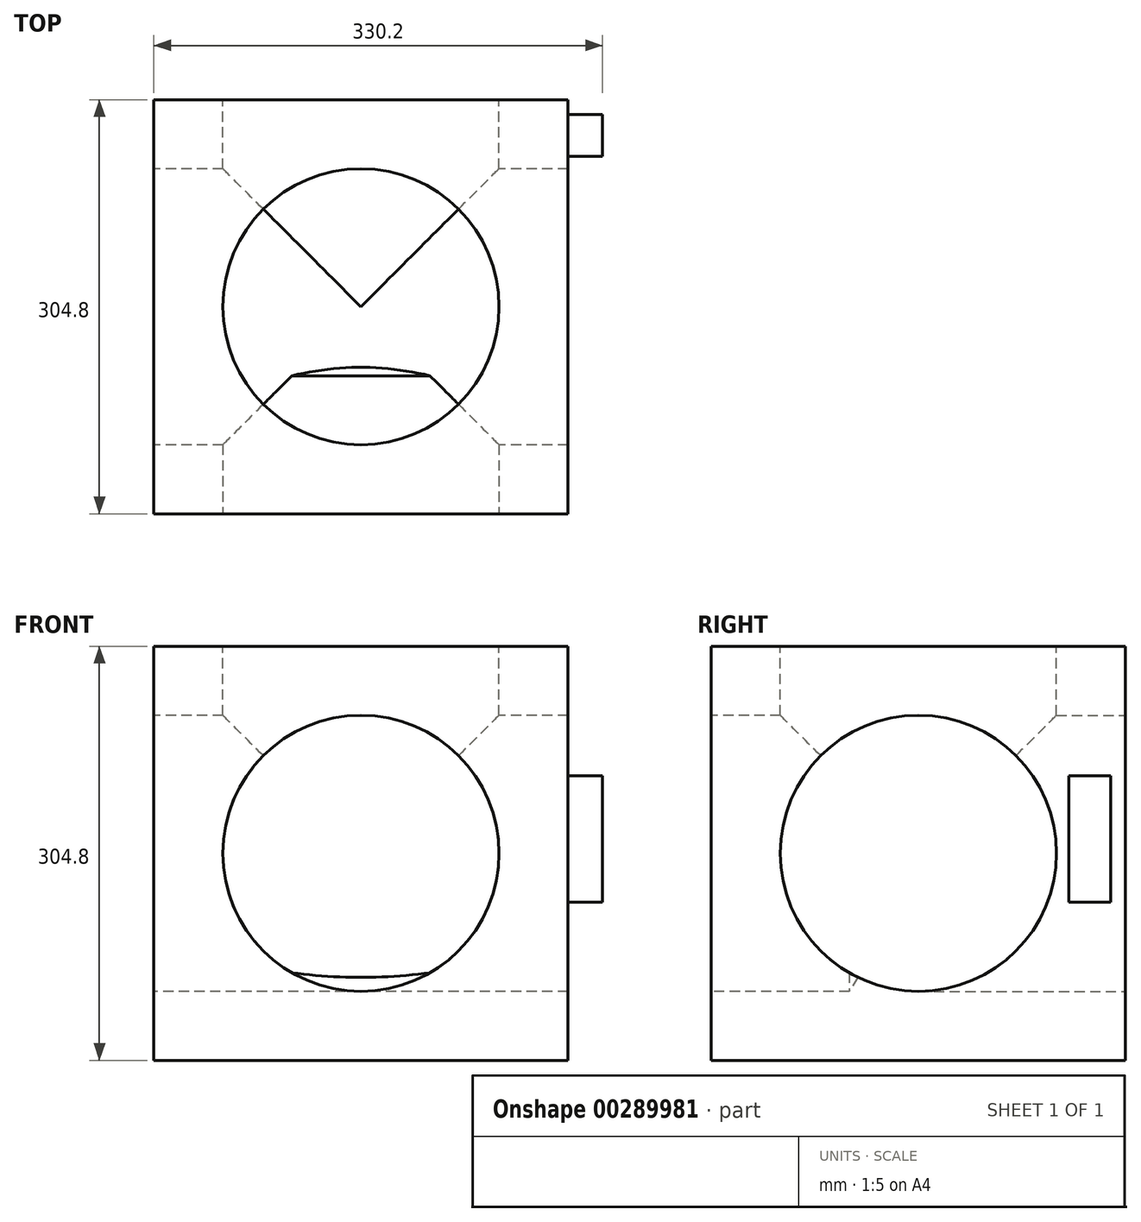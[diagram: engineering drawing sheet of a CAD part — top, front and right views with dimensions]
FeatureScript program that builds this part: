
annotation { "Feature Type Name" : "Feature", "Feature Type Description" : "" }
export const myFeature = defineFeature(function(context is Context, id is Id, definition is map)
    precondition{}
    {
        {
            var Q0;
            Q0=qCreatedBy(makeId("Top.planeOp"),FACE);
            var sketch = newSketch(context, id + "F0", { "sketchPlane" : qUnion([Q0])});
            skLineSegment(sketch, "E0.bottom", {"start": v(-154.31, 197.67) * mm, "end": v(150.49, 197.67) * mm});
            skLineSegment(sketch, "E0.top", {"start": v(-154.31, -107.13) * mm, "end": v(150.49, -107.13) * mm});
            skLineSegment(sketch, "E0.left", {"start": v(-154.31, 197.67) * mm, "end": v(-154.31, -107.13) * mm});
            skLineSegment(sketch, "E0.right", {"start": v(150.49, 197.67) * mm, "end": v(150.49, -107.13) * mm});
            skSolve(sketch);
        }
        {
            var Q0;
            Q0 = qSketchRegion(id + "F0", true);
            extrude(context, id + "F1", {"entities" : qUnion([Q0]), "depth" : 304.8 * mm});
        }
        {
            var Q0;
            Q0=makeQuery(id+"F1.opExtrude","SWEPT_FACE",FACE,{"disambiguationData":[OSD([sQuery(id+"F0.wireOp",EDGE,"E0.top")])]});
            var sketch = newSketch(context, id + "F2", { "sketchPlane" : qUnion([Q0])});
            skCircle(sketch, "E1", {"center": v(-1.91, 152.4) * mm, "radius": 101.6 * mm});
            skSolve(sketch);
        }
        {
            var Q0;
            Q0=sQuery(id+"F2.wireOp",VERTEX,"E1.center");
            var Q1;
            Q1=makeQuery(id+"F1.opExtrude","SWEPT_BODY",BODY,{"disambiguationData":[OSD([sQuery(id+"F0.wireOp",EDGE,"E0.bottom"),sQuery(id+"F0.wireOp",EDGE,"E0.top"),sQuery(id+"F0.wireOp",EDGE,"E0.left"),sQuery(id+"F0.wireOp",EDGE,"E0.right")])]});
            hole(context, id + "F3", {"style" : HoleStyle.SIMPLE, "endStyle" : HoleEndStyle.BLIND, "holeDiameter" : 203.2 * mm, "holeDepth" : 101.6 * mm, "tappedDepth" : 12.7 * mm, "tapClearance" : 3, "startFromSketch" : true, "locations" : qUnion([Q0]), "scope" : qUnion([Q1])});
        }
        {
            var Q0;
            Q0=makeQuery(id+"F1.opExtrude","CAP_FACE",FACE,{"disambiguationData":[OSD([sQuery(id+"F0.wireOp",EDGE,"E0.bottom"),sQuery(id+"F0.wireOp",EDGE,"E0.top"),sQuery(id+"F0.wireOp",EDGE,"E0.left"),sQuery(id+"F0.wireOp",EDGE,"E0.right")])],"isStart":false});
            var sketch = newSketch(context, id + "F4", { "sketchPlane" : qUnion([Q0])});
            skCircle(sketch, "E2", {"center": v(-1.91, 45.27) * mm, "radius": 101.6 * mm});
            skSolve(sketch);
        }
        {
            var Q0;
            Q0=sQuery(id+"F4.wireOp",VERTEX,"E2.center");
            var Q1;
            Q1=makeQuery(id+"F1.opExtrude","SWEPT_BODY",BODY,{"disambiguationData":[OSD([sQuery(id+"F0.wireOp",EDGE,"E0.bottom"),sQuery(id+"F0.wireOp",EDGE,"E0.top"),sQuery(id+"F0.wireOp",EDGE,"E0.left"),sQuery(id+"F0.wireOp",EDGE,"E0.right")])]});
            hole(context, id + "F5", {"style" : HoleStyle.SIMPLE, "endStyle" : HoleEndStyle.BLIND, "holeDiameter" : 203.2 * mm, "holeDepth" : 152.4 * mm, "tappedDepth" : 12.7 * mm, "tapClearance" : 3, "startFromSketch" : true, "locations" : qUnion([Q0]), "scope" : qUnion([Q1])});
        }
        {
            var Q0;
            Q0=makeQuery(id+"F1.opExtrude","SWEPT_FACE",FACE,{"disambiguationData":[OSD([sQuery(id+"F0.wireOp",EDGE,"E0.left")])]});
            var sketch = newSketch(context, id + "F6", { "sketchPlane" : qUnion([Q0])});
            skCircle(sketch, "E3", {"center": v(-45.27, 152.4) * mm, "radius": 101.6 * mm});
            skSolve(sketch);
        }
        {
            var Q0;
            Q0=sQuery(id+"F6.wireOp",VERTEX,"E3.center");
            var Q1;
            Q1=makeQuery(id+"F1.opExtrude","SWEPT_BODY",BODY,{"disambiguationData":[OSD([sQuery(id+"F0.wireOp",EDGE,"E0.bottom"),sQuery(id+"F0.wireOp",EDGE,"E0.top"),sQuery(id+"F0.wireOp",EDGE,"E0.left"),sQuery(id+"F0.wireOp",EDGE,"E0.right")])]});
            hole(context, id + "F7", {"style" : HoleStyle.SIMPLE, "endStyle" : HoleEndStyle.BLIND, "holeDiameter" : 203.2 * mm, "holeDepth" : 152.4 * mm, "tappedDepth" : 12.7 * mm, "tapClearance" : 3, "startFromSketch" : true, "locations" : qUnion([Q0]), "scope" : qUnion([Q1])});
        }
        {
            var Q0;
            Q0=makeQuery(id+"F1.opExtrude","SWEPT_FACE",FACE,{"disambiguationData":[OSD([sQuery(id+"F0.wireOp",EDGE,"E0.bottom")])]});
            var sketch = newSketch(context, id + "F8", { "sketchPlane" : qUnion([Q0])});
            skCircle(sketch, "E4", {"center": v(1.91, 152.4) * mm, "radius": 101.6 * mm});
            skSolve(sketch);
        }
        {
            var Q0;
            Q0=sQuery(id+"F8.wireOp",VERTEX,"E4.center");
            var Q1;
            Q1=makeQuery(id+"F1.opExtrude","SWEPT_BODY",BODY,{"disambiguationData":[OSD([sQuery(id+"F0.wireOp",EDGE,"E0.bottom"),sQuery(id+"F0.wireOp",EDGE,"E0.top"),sQuery(id+"F0.wireOp",EDGE,"E0.left"),sQuery(id+"F0.wireOp",EDGE,"E0.right")])]});
            hole(context, id + "F9", {"style" : HoleStyle.SIMPLE, "endStyle" : HoleEndStyle.BLIND, "holeDiameter" : 203.2 * mm, "holeDepth" : 152.4 * mm, "tappedDepth" : 12.7 * mm, "tapClearance" : 3, "startFromSketch" : true, "locations" : qUnion([Q0]), "scope" : qUnion([Q1])});
        }
        {
            var Q0;
            Q0=makeQuery(id+"F1.opExtrude","SWEPT_FACE",FACE,{"disambiguationData":[OSD([sQuery(id+"F0.wireOp",EDGE,"E0.right")])]});
            var sketch = newSketch(context, id + "F10", { "sketchPlane" : qUnion([Q0])});
            skLineSegment(sketch, "E5.bottom", {"start": v(156.02, 209.32) * mm, "end": v(186.67, 209.32) * mm});
            skLineSegment(sketch, "E5.top", {"start": v(156.02, 116.28) * mm, "end": v(186.67, 116.28) * mm});
            skLineSegment(sketch, "E5.left", {"start": v(156.02, 209.32) * mm, "end": v(156.02, 116.28) * mm});
            skLineSegment(sketch, "E5.right", {"start": v(186.67, 209.32) * mm, "end": v(186.67, 116.28) * mm});
            skSolve(sketch);
        }
        {
            var Q0;
            Q0=makeQuery(id+"F10.imprint","IMPRINT",FACE,{"disambiguationData":[TD([[makeQuery(id+"F10.imprint","IMPRINT",EDGE,{"derivedFrom":sQuery(id+"F10.wireOp",EDGE,"E5.bottom")}),-1.0]])]});
            extrude(context, id + "F11", {"entities" : qUnion([Q0]), "operationType" : NewBodyOperationType.ADD, "depth" : 25.4 * mm});
        }
        {
            var Q0;
            Q0=makeQuery(id+"F1.opExtrude","SWEPT_FACE",FACE,{"disambiguationData":[OSD([sQuery(id+"F0.wireOp",EDGE,"E0.right")])]});
            var sketch = newSketch(context, id + "F12", { "sketchPlane" : qUnion([Q0])});
            skCircle(sketch, "E6", {"center": v(45.27, 152.4) * mm, "radius": 101.6 * mm});
            skSolve(sketch);
        }
        {
            var Q0;
            Q0=sQuery(id+"F12.wireOp",VERTEX,"E6.center");
            var Q1;
            Q1=makeQuery(id+"F1.opExtrude","SWEPT_BODY",BODY,{"disambiguationData":[OSD([sQuery(id+"F0.wireOp",EDGE,"E0.bottom"),sQuery(id+"F0.wireOp",EDGE,"E0.top"),sQuery(id+"F0.wireOp",EDGE,"E0.left"),sQuery(id+"F0.wireOp",EDGE,"E0.right")])]});
            hole(context, id + "F13", {"style" : HoleStyle.SIMPLE, "endStyle" : HoleEndStyle.BLIND, "holeDiameter" : 203.2 * mm, "holeDepth" : 152.4 * mm, "tappedDepth" : 12.7 * mm, "tapClearance" : 3, "startFromSketch" : true, "locations" : qUnion([Q0]), "scope" : qUnion([Q1])});
        }
    });
